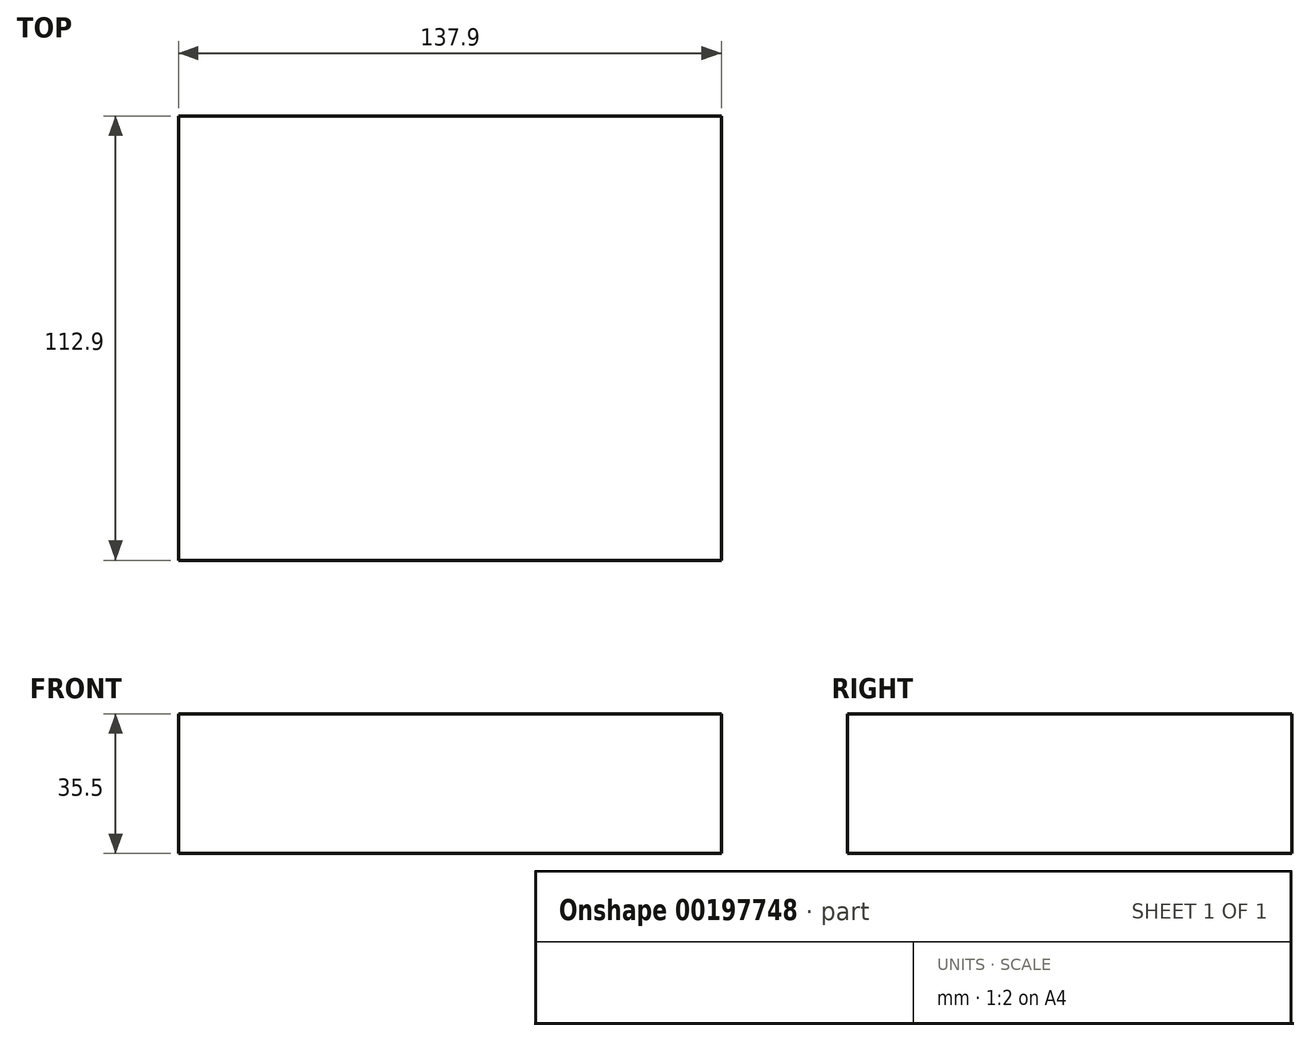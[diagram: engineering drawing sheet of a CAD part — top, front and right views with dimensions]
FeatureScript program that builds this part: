
annotation { "Feature Type Name" : "Feature", "Feature Type Description" : "" }
export const myFeature = defineFeature(function(context is Context, id is Id, definition is map)
    precondition{}
    {
        {
            var Q0;
            Q0=qCreatedBy(makeId("Top.planeOp"),FACE);
            var sketch = newSketch(context, id + "F0", { "sketchPlane" : qUnion([Q0])});
            skLineSegment(sketch, "E0.bottom", {"start": v(-22, -28.62) * mm, "end": v(115.9, -28.62) * mm});
            skLineSegment(sketch, "E0.top", {"start": v(-22, 84.28) * mm, "end": v(115.9, 84.28) * mm});
            skLineSegment(sketch, "E0.left", {"start": v(-22, -28.62) * mm, "end": v(-22, 84.28) * mm});
            skLineSegment(sketch, "E0.right", {"start": v(115.9, -28.62) * mm, "end": v(115.9, 84.28) * mm});
            skSolve(sketch);
        }
        {
            var Q0;
            Q0=makeQuery(id+"F0.imprint","IMPRINT",FACE,{"disambiguationData":[TD([[makeQuery(id+"F0.imprint","IMPRINT",EDGE,{"derivedFrom":sQuery(id+"F0.wireOp",EDGE,"E0.bottom")}),1.0]])]});
            extrude(context, id + "F1", {"entities" : qUnion([Q0]), "depth" : 35.5 * mm});
        }
        {
            var Q0;
            Q0=qCreatedBy(makeId("Top.planeOp"),FACE);
            var sketch = newSketch(context, id + "F2", { "sketchPlane" : qUnion([Q0])});
            skCircle(sketch, "E1", {"center": v(-100.52, 51.13) * mm, "radius": 12.7 * mm});
            skCircle(sketch, "E2", {"center": v(-100.52, 51.13) * mm, "radius": 11.2 * mm});
            skSolve(sketch);
        }
        {
            var Q0;
            Q0=sQuery(id+"F2.wireOp",EDGE,"E2");
            var Q1;
            Q1=sQuery(id+"F2.wireOp",EDGE,"E1");
            extrude(context, id + "F3", {"bodyType" : ToolBodyType.SURFACE, "surfaceEntities" : qUnion([Q0, Q1]), "depth" : 1379 * mm});
        }
    });
